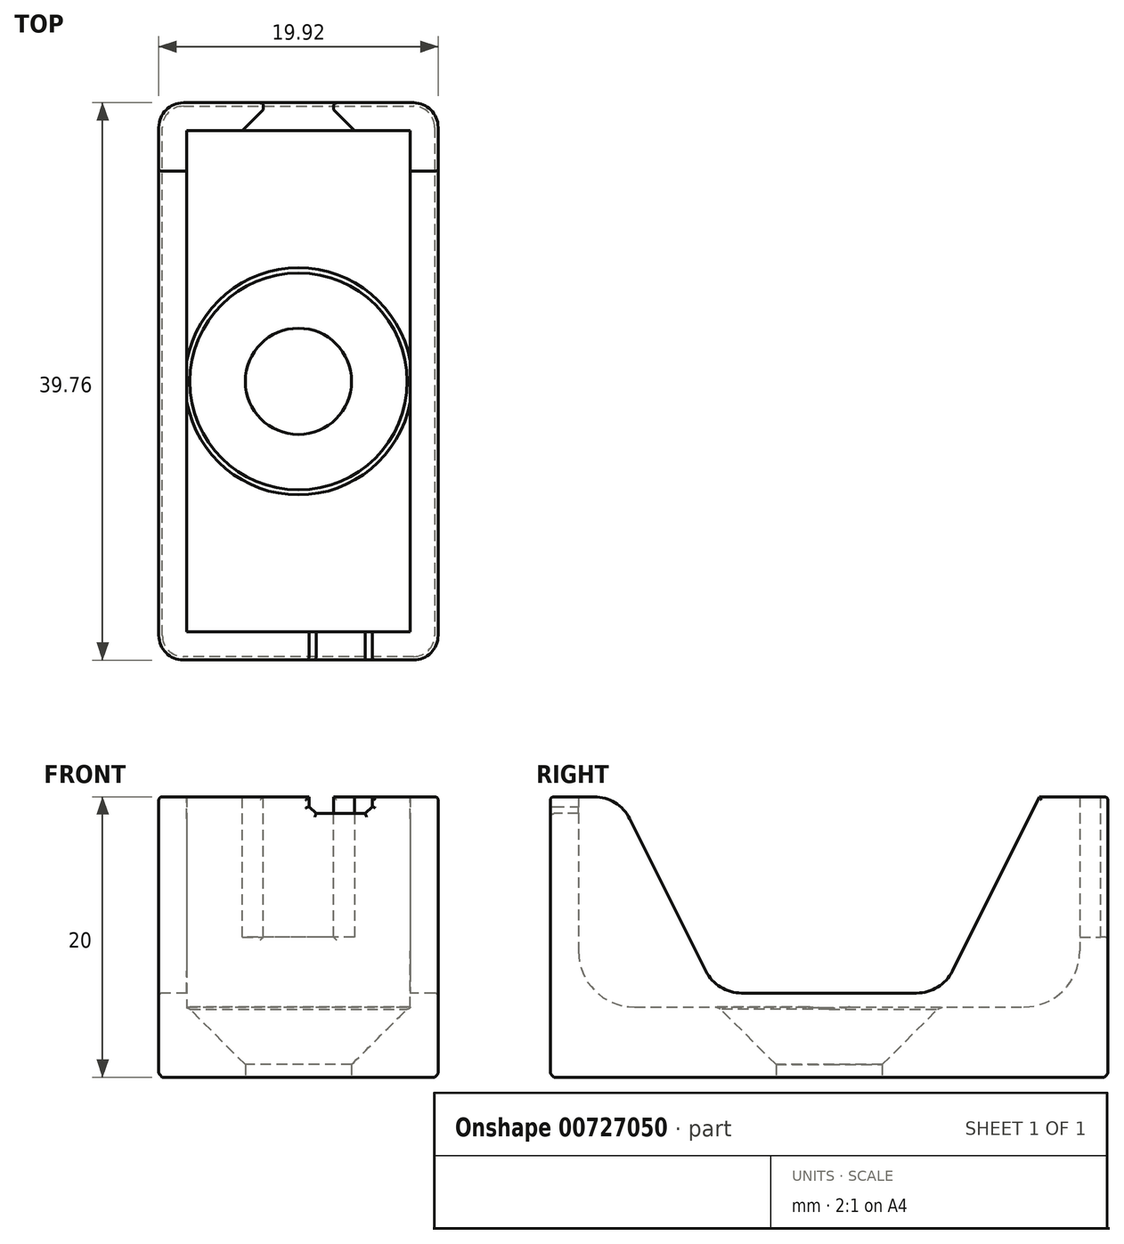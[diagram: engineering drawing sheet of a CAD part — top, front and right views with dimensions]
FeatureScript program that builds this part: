
annotation { "Feature Type Name" : "Feature", "Feature Type Description" : "" }
export const myFeature = defineFeature(function(context is Context, id is Id, definition is map)
    precondition{}
    {
        {
            var Q0;
            Q0=qCreatedBy(makeId("Top.planeOp"),FACE);
            var sketch = newSketch(context, id + "F0", { "sketchPlane" : qUnion([Q0])});
            skLineSegment(sketch, "E0.bottom", {"start": v(7.96, 17.88) * mm, "end": v(-7.96, 17.88) * mm});
            skLineSegment(sketch, "E0.top", {"start": v(7.96, -17.88) * mm, "end": v(-7.96, -17.88) * mm});
            skLineSegment(sketch, "E0.left", {"start": v(7.96, 17.88) * mm, "end": v(7.96, -17.88) * mm});
            skLineSegment(sketch, "E0.right", {"start": v(-7.96, 17.88) * mm, "end": v(-7.96, -17.88) * mm});
            skPoint(sketch, "E0.middle", {"position": v(0, 0) * mm});
            skLineSegment(sketch, "E1.0", {"start": v(9.96, 19.88) * mm, "end": v(-9.96, 19.88) * mm});
            skLineSegment(sketch, "E1.1", {"start": v(9.96, 19.88) * mm, "end": v(9.96, -19.88) * mm});
            skLineSegment(sketch, "E1.2", {"start": v(9.96, -19.88) * mm, "end": v(-9.96, -19.88) * mm});
            skLineSegment(sketch, "E1.3", {"start": v(-9.96, 19.88) * mm, "end": v(-9.96, -19.88) * mm});
            skCircle(sketch, "E2", {"center": v(0, 0) * mm, "radius": 3.8 * mm});
            skSolve(sketch);
        }
        {
            var Q0;
            Q0=makeQuery(id+"F0.imprint","IMPRINT",FACE,{"disambiguationData":[TD([[makeQuery(id+"F0.imprint","IMPRINT",EDGE,{"derivedFrom":sQuery(id+"F0.wireOp",EDGE,"E0.bottom")}),1.0]])]});
            var Q1;
            Q1=makeQuery(id+"F0.imprint","IMPRINT",FACE,{"disambiguationData":[TD([[makeQuery(id+"F0.imprint","IMPRINT",EDGE,{"derivedFrom":sQuery(id+"F0.wireOp",EDGE,"E0.bottom")}),-1.0]])]});
            extrude(context, id + "F1", {"entities" : qUnion([Q0, Q1]), "depth" : 5 * mm, "offsetDistance" : 25 * mm});
        }
        {
            var Q0;
            Q0=makeQuery(id+"F0.imprint","IMPRINT",FACE,{"disambiguationData":[TD([[makeQuery(id+"F0.imprint","IMPRINT",EDGE,{"derivedFrom":sQuery(id+"F0.wireOp",EDGE,"E0.bottom")}),-1.0]])]});
            extrude(context, id + "F2", {"entities" : qUnion([Q0]), "operationType" : NewBodyOperationType.ADD, "depth" : 20 * mm, "offsetDistance" : 25 * mm});
        }
        {
            var Q0;
            Q0=makeQuery(id+"F1.opExtrude","CAP_FACE",FACE,{"disambiguationData":[OSD([sQuery(id+"F0.wireOp",EDGE,"E1.0"),sQuery(id+"F0.wireOp",EDGE,"E1.1"),sQuery(id+"F0.wireOp",EDGE,"E1.2"),sQuery(id+"F0.wireOp",EDGE,"E1.3"),sQuery(id+"F0.wireOp",EDGE,"E2")])],"isStart":false});
            var sketch = newSketch(context, id + "F3", { "sketchPlane" : qUnion([Q0])});
            skLineSegment(sketch, "E3", {"start": v(7.96, -17.88) * mm, "end": v(5.26, -17.88) * mm});
            skLineSegment(sketch, "E4", {"start": v(5.26, -17.88) * mm, "end": v(0.76, -17.88) * mm});
            skLineSegment(sketch, "E5", {"start": v(0.76, -17.88) * mm, "end": v(0.76, -20.5) * mm});
            skLineSegment(sketch, "E6", {"start": v(0.76, -20.5) * mm, "end": v(5.26, -20.5) * mm});
            skLineSegment(sketch, "E7", {"start": v(5.26, -20.5) * mm, "end": v(5.26, -17.88) * mm});
            skSolve(sketch);
        }
        {
            var Q0;
            Q0 = qSketchRegion(id + "F3", true);
            extrude(context, id + "F4", {"entities" : qUnion([Q0]), "operationType" : NewBodyOperationType.REMOVE, "depth" : 35.9 * mm, "offsetDistance" : 25 * mm, "hasSecondDirection" : true, "secondDirectionOppositeDirection" : false, "secondDirectionDepth" : 13.8 * mm});
        }
        {
            var Q0;
            Q0=makeQuery(id+"F1.opExtrude","CAP_FACE",FACE,{"disambiguationData":[OSD([sQuery(id+"F0.wireOp",EDGE,"E1.0"),sQuery(id+"F0.wireOp",EDGE,"E1.1"),sQuery(id+"F0.wireOp",EDGE,"E1.2"),sQuery(id+"F0.wireOp",EDGE,"E1.3"),sQuery(id+"F0.wireOp",EDGE,"E2")])],"isStart":false});
            var sketch = newSketch(context, id + "F5", { "sketchPlane" : qUnion([Q0])});
            skLineSegment(sketch, "E8.bottom", {"start": v(2.5, 20.25) * mm, "end": v(-2.5, 20.25) * mm});
            skLineSegment(sketch, "E8.top", {"start": v(2.5, 17.25) * mm, "end": v(-2.5, 17.25) * mm});
            skLineSegment(sketch, "E8.left", {"start": v(2.5, 20.25) * mm, "end": v(2.5, 17.25) * mm});
            skLineSegment(sketch, "E8.right", {"start": v(-2.5, 20.25) * mm, "end": v(-2.5, 17.25) * mm});
            skPoint(sketch, "E8.middle", {"position": v(0, 18.75) * mm});
            skSolve(sketch);
        }
        {
            var Q0;
            Q0 = qSketchRegion(id + "F5", true);
            extrude(context, id + "F6", {"entities" : qUnion([Q0]), "operationType" : NewBodyOperationType.REMOVE, "depth" : 20 * mm, "offsetDistance" : 25 * mm, "hasSecondDirection" : true, "secondDirectionOppositeDirection" : false, "secondDirectionDepth" : 5 * mm});
        }
        {
            var Q0;
            {var subQ0=sQuery(id+"F0.wireOp",EDGE,"E1.3");Q0=makeQuery(id+"F2.boolean.opBoolean","MERGE",FACE,{"derivedFrom":[makeQuery(id+"F1.opExtrude","SWEPT_FACE",FACE,{"disambiguationData":[OSD([subQ0])]}),makeQuery(id+"F2.opExtrude","SWEPT_FACE",FACE,{"disambiguationData":[OSD([subQ0])]})]});}
            var sketch = newSketch(context, id + "F7", { "sketchPlane" : qUnion([Q0])});
            skLineSegment(sketch, "E9", {"start": v(0, 0) * mm, "end": v(0, 6) * mm});
            skLineSegment(sketch, "E10", {"start": v(0, 20) * mm, "end": v(-15, 20) * mm});
            skLineSegment(sketch, "E11", {"start": v(0, 20) * mm, "end": v(15, 20) * mm});
            skLineSegment(sketch, "E12", {"start": v(0, 6) * mm, "end": v(8, 6) * mm});
            skLineSegment(sketch, "E13", {"start": v(8, 6) * mm, "end": v(15, 20) * mm});
            skLineSegment(sketch, "E14", {"start": v(0, 6) * mm, "end": v(-8, 6) * mm});
            skLineSegment(sketch, "E15", {"start": v(-8, 6) * mm, "end": v(-15, 20) * mm});
            skSolve(sketch);
        }
        {
            var Q0;
            Q0=makeQuery(id+"F7.imprint","IMPRINT",FACE,{"disambiguationData":[TD([[makeQuery(id+"F7.imprint","IMPRINT",EDGE,{"derivedFrom":sQuery(id+"F7.wireOp",EDGE,"E10")}),-1.0]])]});
            extrude(context, id + "F8", {"entities" : qUnion([Q0]), "operationType" : NewBodyOperationType.REMOVE, "oppositeDirection" : true, "depth" : 25 * mm, "offsetDistance" : 25 * mm});
        }
        {
            var Q0;
            Q0=makeQuery(id+"F1.opExtrude","CAP_EDGE",EDGE,{"disambiguationData":[OSD([sQuery(id+"F0.wireOp",EDGE,"E2")])],"isStart":false});
            chamfer(context, id + "F9", {"entities" : qUnion([Q0]), "width" : 4.1 * mm, "tangentPropagation" : true});
        }
        {
            var Q0;
            {var subQ0=sQuery(id+"F0.wireOp",EDGE,"E1.3");var subQ1=sQuery(id+"F0.wireOp",EDGE,"E1.0");Q0=makeQuery(id+"F2.boolean.opBoolean","MERGE",EDGE,{"derivedFrom":[makeQuery(id+"F1.opExtrude","SWEPT_EDGE",EDGE,{"disambiguationData":[OSD([subQ1,subQ0])]}),makeQuery(id+"F2.opExtrude","SWEPT_EDGE",EDGE,{"disambiguationData":[OSD([subQ1,subQ0])]})]});}
            var Q1;
            {var subQ0=sQuery(id+"F0.wireOp",EDGE,"E1.1");var subQ1=sQuery(id+"F0.wireOp",EDGE,"E1.0");Q1=makeQuery(id+"F2.boolean.opBoolean","MERGE",EDGE,{"derivedFrom":[makeQuery(id+"F1.opExtrude","SWEPT_EDGE",EDGE,{"disambiguationData":[OSD([subQ1,subQ0])]}),makeQuery(id+"F2.opExtrude","SWEPT_EDGE",EDGE,{"disambiguationData":[OSD([subQ1,subQ0])]})]});}
            var Q2;
            {var subQ0=sQuery(id+"F0.wireOp",EDGE,"E1.2");var subQ1=sQuery(id+"F0.wireOp",EDGE,"E1.1");Q2=makeQuery(id+"F2.boolean.opBoolean","MERGE",EDGE,{"derivedFrom":[makeQuery(id+"F1.opExtrude","SWEPT_EDGE",EDGE,{"disambiguationData":[OSD([subQ1,subQ0])]}),makeQuery(id+"F2.opExtrude","SWEPT_EDGE",EDGE,{"disambiguationData":[OSD([subQ1,subQ0])]})]});}
            var Q3;
            {var subQ0=sQuery(id+"F0.wireOp",EDGE,"E1.3");var subQ1=sQuery(id+"F0.wireOp",EDGE,"E1.2");Q3=makeQuery(id+"F2.boolean.opBoolean","MERGE",EDGE,{"derivedFrom":[makeQuery(id+"F1.opExtrude","SWEPT_EDGE",EDGE,{"disambiguationData":[OSD([subQ1,subQ0])]}),makeQuery(id+"F2.opExtrude","SWEPT_EDGE",EDGE,{"disambiguationData":[OSD([subQ1,subQ0])]})]});}
            fillet(context, id + "F10", {"entities" : qUnion([Q0, Q1, Q2, Q3]), "radius" : 1.75 * mm, "tangentPropagation" : true, "allowEdgeOverflow" : false});
        }
        {
            var Q0;
            Q0=makeQuery(id+"F2.boolean.opBoolean","INTERSECT",EDGE,{"derivedFrom":[makeQuery(id+"F1.opExtrude","CAP_FACE",FACE,{"disambiguationData":[OSD([sQuery(id+"F0.wireOp",EDGE,"E1.0"),sQuery(id+"F0.wireOp",EDGE,"E1.1"),sQuery(id+"F0.wireOp",EDGE,"E1.2"),sQuery(id+"F0.wireOp",EDGE,"E1.3"),sQuery(id+"F0.wireOp",EDGE,"E2")])],"isStart":false}),makeQuery(id+"F2.opExtrude","SWEPT_FACE",FACE,{"disambiguationData":[OSD([sQuery(id+"F0.wireOp",EDGE,"E0.bottom")])]})]});
            var Q1;
            Q1=makeQuery(id+"F2.boolean.opBoolean","INTERSECT",EDGE,{"derivedFrom":[makeQuery(id+"F1.opExtrude","CAP_FACE",FACE,{"disambiguationData":[OSD([sQuery(id+"F0.wireOp",EDGE,"E1.0"),sQuery(id+"F0.wireOp",EDGE,"E1.1"),sQuery(id+"F0.wireOp",EDGE,"E1.2"),sQuery(id+"F0.wireOp",EDGE,"E1.3"),sQuery(id+"F0.wireOp",EDGE,"E2")])],"isStart":false}),makeQuery(id+"F2.opExtrude","SWEPT_FACE",FACE,{"disambiguationData":[OSD([sQuery(id+"F0.wireOp",EDGE,"E0.top")])]})]});
            fillet(context, id + "F11", {"entities" : qUnion([Q0, Q1]), "radius" : 4 * mm, "tangentPropagation" : true, "allowEdgeOverflow" : false});
        }
        {
            var Q0;
            Q0=makeQuery(id+"F4.boolean.opBoolean","COPY",EDGE,{"derivedFrom":makeQuery(id+"F4.opExtrude","CAP_EDGE",EDGE,{"disambiguationData":[OSD([sQuery(id+"F3.wireOp",EDGE,"E5")])],"isStart":true})});
            var Q1;
            Q1=makeQuery(id+"F4.boolean.opBoolean","COPY",EDGE,{"derivedFrom":makeQuery(id+"F4.opExtrude","CAP_EDGE",EDGE,{"disambiguationData":[OSD([sQuery(id+"F3.wireOp",EDGE,"E7")])],"isStart":true})});
            var Q2;
            {var subQ0=sQuery(id+"F0.wireOp",EDGE,"E2");Q2=makeQuery(id+"F9.opChamfer","BLEND_EDGE",EDGE,{"blendedFrom":[makeQuery(id+"F1.opExtrude","CAP_EDGE",EDGE,{"disambiguationData":[OSD([subQ0])],"isStart":false}),makeQuery(id+"F1.opExtrude","CAP_FACE",FACE,{"disambiguationData":[OSD([sQuery(id+"F0.wireOp",EDGE,"E1.0"),sQuery(id+"F0.wireOp",EDGE,"E1.1"),sQuery(id+"F0.wireOp",EDGE,"E1.2"),sQuery(id+"F0.wireOp",EDGE,"E1.3"),subQ0])],"isStart":false})],"blendedInto":[makeQuery(id+"F1.opExtrude","CAP_FACE",FACE,{"disambiguationData":[OSD([sQuery(id+"F0.wireOp",EDGE,"E1.0"),sQuery(id+"F0.wireOp",EDGE,"E1.1"),sQuery(id+"F0.wireOp",EDGE,"E1.2"),sQuery(id+"F0.wireOp",EDGE,"E1.3"),subQ0])],"isStart":false})]});}
            chamfer(context, id + "F12", {"entities" : qUnion([Q0, Q1, Q2]), "width" : .5 * mm, "tangentPropagation" : true});
        }
        {
            var Q0;
            Q0=makeQuery(id+"F6.boolean.opBoolean","INTERSECT",EDGE,{"derivedFrom":[makeQuery(id+"F2.opExtrude","SWEPT_FACE",FACE,{"disambiguationData":[OSD([sQuery(id+"F0.wireOp",EDGE,"E0.bottom")])]}),makeQuery(id+"F6.opExtrude","SWEPT_FACE",FACE,{"disambiguationData":[OSD([sQuery(id+"F5.wireOp",EDGE,"E8.right")])]})]});
            var Q1;
            Q1=makeQuery(id+"F6.boolean.opBoolean","INTERSECT",EDGE,{"derivedFrom":[makeQuery(id+"F2.opExtrude","SWEPT_FACE",FACE,{"disambiguationData":[OSD([sQuery(id+"F0.wireOp",EDGE,"E0.bottom")])]}),makeQuery(id+"F6.opExtrude","SWEPT_FACE",FACE,{"disambiguationData":[OSD([sQuery(id+"F5.wireOp",EDGE,"E8.left")])]})]});
            chamfer(context, id + "F13", {"entities" : qUnion([Q0, Q1]), "width" : 1.5 * mm, "tangentPropagation" : true});
        }
        {
            var Q0;
            {var subQ0=sQuery(id+"F7.wireOp",EDGE,"E12");var subQ1=sQuery(id+"F0.wireOp",EDGE,"E1.3");var subQ2=sQuery(id+"F7.wireOp",EDGE,"E13");Q0=makeQuery(id+"F8.boolean.opBoolean","COPY",EDGE,{"disambiguationData":[TD([makeQuery(id+"F1.opExtrude","SWEPT_FACE",FACE,{"disambiguationData":[OSD([subQ1])]})])],"derivedFrom":makeQuery(id+"F8.opExtrude","SWEPT_EDGE",EDGE,{"disambiguationData":[OSD([subQ0,subQ2])]})});}
            var Q1;
            {var subQ1=sQuery(id+"F0.wireOp",EDGE,"E1.3");var subQ2=sQuery(id+"F7.wireOp",EDGE,"E13");Q1=makeQuery(id+"F8.boolean.opBoolean","COPY",EDGE,{"disambiguationData":[TD([makeQuery(id+"F1.opExtrude","SWEPT_FACE",FACE,{"disambiguationData":[OSD([subQ1])]})])],"derivedFrom":makeQuery(id+"F8.opExtrude","SWEPT_EDGE",EDGE,{"disambiguationData":[OSD([subQ1,sQuery(id+"F7.wireOp",EDGE,"E11"),subQ2])]})});}
            var Q2;
            {var subQ1=sQuery(id+"F0.wireOp",EDGE,"E1.1");var subQ2=sQuery(id+"F0.wireOp",EDGE,"E1.3");var subQ3=sQuery(id+"F7.wireOp",EDGE,"E13");Q2=makeQuery(id+"F8.boolean.opBoolean","COPY",EDGE,{"disambiguationData":[TD([makeQuery(id+"F1.opExtrude","SWEPT_FACE",FACE,{"disambiguationData":[OSD([subQ1])]})])],"derivedFrom":makeQuery(id+"F8.opExtrude","SWEPT_EDGE",EDGE,{"disambiguationData":[OSD([subQ2,sQuery(id+"F7.wireOp",EDGE,"E11"),subQ3])]})});}
            var Q3;
            {var subQ0=sQuery(id+"F7.wireOp",EDGE,"E12");var subQ1=sQuery(id+"F0.wireOp",EDGE,"E1.1");var subQ2=sQuery(id+"F7.wireOp",EDGE,"E13");Q3=makeQuery(id+"F8.boolean.opBoolean","COPY",EDGE,{"disambiguationData":[TD([makeQuery(id+"F1.opExtrude","SWEPT_FACE",FACE,{"disambiguationData":[OSD([subQ1])]})])],"derivedFrom":makeQuery(id+"F8.opExtrude","SWEPT_EDGE",EDGE,{"disambiguationData":[OSD([subQ0,subQ2])]})});}
            var Q4;
            {var subQ0=sQuery(id+"F7.wireOp",EDGE,"E14");var subQ1=sQuery(id+"F0.wireOp",EDGE,"E1.1");var subQ2=sQuery(id+"F7.wireOp",EDGE,"E15");Q4=makeQuery(id+"F8.boolean.opBoolean","COPY",EDGE,{"disambiguationData":[TD([makeQuery(id+"F1.opExtrude","SWEPT_FACE",FACE,{"disambiguationData":[OSD([subQ1])]})])],"derivedFrom":makeQuery(id+"F8.opExtrude","SWEPT_EDGE",EDGE,{"disambiguationData":[OSD([subQ0,subQ2])]})});}
            var Q5;
            {var subQ0=sQuery(id+"F7.wireOp",EDGE,"E14");var subQ1=sQuery(id+"F0.wireOp",EDGE,"E1.3");var subQ2=sQuery(id+"F7.wireOp",EDGE,"E15");Q5=makeQuery(id+"F8.boolean.opBoolean","COPY",EDGE,{"disambiguationData":[TD([makeQuery(id+"F1.opExtrude","SWEPT_FACE",FACE,{"disambiguationData":[OSD([subQ1])]})])],"derivedFrom":makeQuery(id+"F8.opExtrude","SWEPT_EDGE",EDGE,{"disambiguationData":[OSD([subQ0,subQ2])]})});}
            var Q6;
            {var subQ1=sQuery(id+"F0.wireOp",EDGE,"E1.3");var subQ2=sQuery(id+"F7.wireOp",EDGE,"E15");Q6=makeQuery(id+"F8.boolean.opBoolean","COPY",EDGE,{"disambiguationData":[TD([makeQuery(id+"F1.opExtrude","SWEPT_FACE",FACE,{"disambiguationData":[OSD([subQ1])]})])],"derivedFrom":makeQuery(id+"F8.opExtrude","SWEPT_EDGE",EDGE,{"disambiguationData":[OSD([subQ1,sQuery(id+"F7.wireOp",EDGE,"E10"),subQ2])]})});}
            var Q7;
            {var subQ1=sQuery(id+"F0.wireOp",EDGE,"E1.1");var subQ2=sQuery(id+"F0.wireOp",EDGE,"E1.3");var subQ3=sQuery(id+"F7.wireOp",EDGE,"E15");Q7=makeQuery(id+"F8.boolean.opBoolean","COPY",EDGE,{"disambiguationData":[TD([makeQuery(id+"F1.opExtrude","SWEPT_FACE",FACE,{"disambiguationData":[OSD([subQ1])]})])],"derivedFrom":makeQuery(id+"F8.opExtrude","SWEPT_EDGE",EDGE,{"disambiguationData":[OSD([subQ2,sQuery(id+"F7.wireOp",EDGE,"E10"),subQ3])]})});}
            fillet(context, id + "F14", {"entities" : qUnion([Q0, Q1, Q2, Q3, Q4, Q5, Q6, Q7]), "radius" : 2.85 * mm, "tangentPropagation" : true, "allowEdgeOverflow" : false});
        }
        {
            var Q0;
            {var subQ0=sQuery(id+"F0.wireOp",EDGE,"E1.2");var subQ1=sQuery(id+"F0.wireOp",EDGE,"E1.1");Q0=makeQuery(id+"F10.opFillet","BLEND_EDGE",EDGE,{"blendedFrom":[makeQuery(id+"F2.boolean.opBoolean","MERGE",EDGE,{"derivedFrom":[makeQuery(id+"F1.opExtrude","SWEPT_EDGE",EDGE,{"disambiguationData":[OSD([subQ1,subQ0])]}),makeQuery(id+"F2.opExtrude","SWEPT_EDGE",EDGE,{"disambiguationData":[OSD([subQ1,subQ0])]})]}),makeQuery(id+"F1.opExtrude","CAP_FACE",FACE,{"disambiguationData":[OSD([sQuery(id+"F0.wireOp",EDGE,"E1.0"),subQ1,subQ0,sQuery(id+"F0.wireOp",EDGE,"E1.3"),sQuery(id+"F0.wireOp",EDGE,"E2")])],"isStart":true})],"blendedInto":[makeQuery(id+"F1.opExtrude","CAP_FACE",FACE,{"disambiguationData":[OSD([sQuery(id+"F0.wireOp",EDGE,"E1.0"),subQ1,subQ0,sQuery(id+"F0.wireOp",EDGE,"E1.3"),sQuery(id+"F0.wireOp",EDGE,"E2")])],"isStart":true})]});}
            var Q1;
            Q1=makeQuery(id+"F1.opExtrude","CAP_EDGE",EDGE,{"disambiguationData":[OSD([sQuery(id+"F0.wireOp",EDGE,"E1.1")])],"isStart":true});
            var Q2;
            Q2=makeQuery(id+"F1.opExtrude","CAP_EDGE",EDGE,{"disambiguationData":[OSD([sQuery(id+"F0.wireOp",EDGE,"E1.2")])],"isStart":true});
            var Q3;
            {var subQ0=sQuery(id+"F0.wireOp",EDGE,"E1.3");var subQ1=sQuery(id+"F0.wireOp",EDGE,"E1.2");Q3=makeQuery(id+"F10.opFillet","BLEND_EDGE",EDGE,{"blendedFrom":[makeQuery(id+"F2.boolean.opBoolean","MERGE",EDGE,{"derivedFrom":[makeQuery(id+"F1.opExtrude","SWEPT_EDGE",EDGE,{"disambiguationData":[OSD([subQ1,subQ0])]}),makeQuery(id+"F2.opExtrude","SWEPT_EDGE",EDGE,{"disambiguationData":[OSD([subQ1,subQ0])]})]}),makeQuery(id+"F1.opExtrude","CAP_FACE",FACE,{"disambiguationData":[OSD([sQuery(id+"F0.wireOp",EDGE,"E1.0"),sQuery(id+"F0.wireOp",EDGE,"E1.1"),subQ1,subQ0,sQuery(id+"F0.wireOp",EDGE,"E2")])],"isStart":true})],"blendedInto":[makeQuery(id+"F1.opExtrude","CAP_FACE",FACE,{"disambiguationData":[OSD([sQuery(id+"F0.wireOp",EDGE,"E1.0"),sQuery(id+"F0.wireOp",EDGE,"E1.1"),subQ1,subQ0,sQuery(id+"F0.wireOp",EDGE,"E2")])],"isStart":true})]});}
            var Q4;
            Q4=makeQuery(id+"F1.opExtrude","CAP_EDGE",EDGE,{"disambiguationData":[OSD([sQuery(id+"F0.wireOp",EDGE,"E1.3")])],"isStart":true});
            var Q5;
            Q5=makeQuery(id+"F1.opExtrude","CAP_EDGE",EDGE,{"disambiguationData":[OSD([sQuery(id+"F0.wireOp",EDGE,"E1.0")])],"isStart":true});
            var Q6;
            {var subQ0=sQuery(id+"F0.wireOp",EDGE,"E1.3");var subQ1=sQuery(id+"F0.wireOp",EDGE,"E1.0");Q6=makeQuery(id+"F10.opFillet","BLEND_EDGE",EDGE,{"blendedFrom":[makeQuery(id+"F2.boolean.opBoolean","MERGE",EDGE,{"derivedFrom":[makeQuery(id+"F1.opExtrude","SWEPT_EDGE",EDGE,{"disambiguationData":[OSD([subQ1,subQ0])]}),makeQuery(id+"F2.opExtrude","SWEPT_EDGE",EDGE,{"disambiguationData":[OSD([subQ1,subQ0])]})]}),makeQuery(id+"F1.opExtrude","CAP_FACE",FACE,{"disambiguationData":[OSD([subQ1,sQuery(id+"F0.wireOp",EDGE,"E1.1"),sQuery(id+"F0.wireOp",EDGE,"E1.2"),subQ0,sQuery(id+"F0.wireOp",EDGE,"E2")])],"isStart":true})],"blendedInto":[makeQuery(id+"F1.opExtrude","CAP_FACE",FACE,{"disambiguationData":[OSD([subQ1,sQuery(id+"F0.wireOp",EDGE,"E1.1"),sQuery(id+"F0.wireOp",EDGE,"E1.2"),subQ0,sQuery(id+"F0.wireOp",EDGE,"E2")])],"isStart":true})]});}
            chamfer(context, id + "F15", {"entities" : qUnion([Q0, Q1, Q2, Q3, Q4, Q5, Q6]), "width" : .25 * mm, "tangentPropagation" : true});
        }
        {
            var Q0;
            {var subQ0=sQuery(id+"F0.wireOp",EDGE,"E1.3");var subQ1=sQuery(id+"F0.wireOp",EDGE,"E1.2");Q0=makeQuery(id+"F4.boolean.opBoolean","SPLIT",EDGE,{"disambiguationData":[TD([makeQuery(id+"F1.opExtrude","SWEPT_FACE",FACE,{"disambiguationData":[OSD([subQ0])]})])],"derivedFrom":makeQuery(id+"F2.opExtrude","CAP_EDGE",EDGE,{"disambiguationData":[OSD([subQ1])],"isStart":false})});}
            var Q1;
            {var subQ0=sQuery(id+"F0.wireOp",EDGE,"E0.right");var subQ2=sQuery(id+"F0.wireOp",EDGE,"E1.3");var subQ3=makeQuery(id+"F1.opExtrude","SWEPT_FACE",FACE,{"disambiguationData":[OSD([subQ2])]});var subQ4=sQuery(id+"F0.wireOp",EDGE,"E0.top");var subQ6=sQuery(id+"F0.wireOp",EDGE,"E1.2");var subQ7=makeQuery(id+"F1.opExtrude","SWEPT_FACE",FACE,{"disambiguationData":[OSD([subQ6])]});var subQ11=sQuery(id+"F0.wireOp",EDGE,"E0.bottom");var subQ12=sQuery(id+"F0.wireOp",EDGE,"E1.0");Q1=makeQuery(id+"F10.opFillet","BLEND_EDGE",EDGE,{"blendedFrom":[makeQuery(id+"F2.boolean.opBoolean","MERGE",EDGE,{"derivedFrom":[makeQuery(id+"F1.opExtrude","SWEPT_EDGE",EDGE,{"disambiguationData":[OSD([subQ6,subQ2])]}),makeQuery(id+"F2.opExtrude","SWEPT_EDGE",EDGE,{"disambiguationData":[OSD([subQ6,subQ2])]})]}),makeQuery(id+"F8.boolean.opBoolean","SPLIT",FACE,{"disambiguationData":[TD([subQ7])],"derivedFrom":makeQuery(id+"F6.boolean.opBoolean","SPLIT",FACE,{"disambiguationData":[TD([subQ3])],"derivedFrom":makeQuery(id+"F2.opExtrude","CAP_FACE",FACE,{"disambiguationData":[OSD([subQ11,subQ4,sQuery(id+"F0.wireOp",EDGE,"E0.left"),subQ0,subQ12,sQuery(id+"F0.wireOp",EDGE,"E1.1"),subQ6,subQ2])],"isStart":false})})})],"blendedInto":[makeQuery(id+"F8.boolean.opBoolean","SPLIT",FACE,{"disambiguationData":[TD([subQ7])],"derivedFrom":makeQuery(id+"F6.boolean.opBoolean","SPLIT",FACE,{"disambiguationData":[TD([subQ3])],"derivedFrom":makeQuery(id+"F2.opExtrude","CAP_FACE",FACE,{"disambiguationData":[OSD([subQ11,subQ4,sQuery(id+"F0.wireOp",EDGE,"E0.left"),subQ0,subQ12,sQuery(id+"F0.wireOp",EDGE,"E1.1"),subQ6,subQ2])],"isStart":false})})})]});}
            var Q2;
            {var subQ0=sQuery(id+"F0.wireOp",EDGE,"E1.2");Q2=makeQuery(id+"F4.boolean.opBoolean","INTERSECT",EDGE,{"derivedFrom":[makeQuery(id+"F2.boolean.opBoolean","MERGE",FACE,{"derivedFrom":[makeQuery(id+"F1.opExtrude","SWEPT_FACE",FACE,{"disambiguationData":[OSD([subQ0])]}),makeQuery(id+"F2.opExtrude","SWEPT_FACE",FACE,{"disambiguationData":[OSD([subQ0])]})]}),makeQuery(id+"F4.opExtrude","SWEPT_FACE",FACE,{"disambiguationData":[OSD([sQuery(id+"F3.wireOp",EDGE,"E5")])]})]});}
            var Q3;
            {var subQ0=sQuery(id+"F0.wireOp",EDGE,"E1.2");var subQ1=sQuery(id+"F0.wireOp",EDGE,"E1.1");Q3=makeQuery(id+"F4.boolean.opBoolean","SPLIT",EDGE,{"disambiguationData":[TD([makeQuery(id+"F1.opExtrude","SWEPT_FACE",FACE,{"disambiguationData":[OSD([subQ1])]})])],"derivedFrom":makeQuery(id+"F2.opExtrude","CAP_EDGE",EDGE,{"disambiguationData":[OSD([subQ0])],"isStart":false})});}
            var Q4;
            {var subQ0=sQuery(id+"F0.wireOp",EDGE,"E1.2");Q4=makeQuery(id+"F12.opChamfer","BLEND_EDGE",EDGE,{"blendedFrom":[makeQuery(id+"F4.boolean.opBoolean","COPY",EDGE,{"derivedFrom":makeQuery(id+"F4.opExtrude","CAP_EDGE",EDGE,{"disambiguationData":[OSD([sQuery(id+"F3.wireOp",EDGE,"E5")])],"isStart":true})}),makeQuery(id+"F2.boolean.opBoolean","MERGE",FACE,{"derivedFrom":[makeQuery(id+"F1.opExtrude","SWEPT_FACE",FACE,{"disambiguationData":[OSD([subQ0])]}),makeQuery(id+"F2.opExtrude","SWEPT_FACE",FACE,{"disambiguationData":[OSD([subQ0])]})]})],"blendedInto":[makeQuery(id+"F2.boolean.opBoolean","MERGE",FACE,{"derivedFrom":[makeQuery(id+"F1.opExtrude","SWEPT_FACE",FACE,{"disambiguationData":[OSD([subQ0])]}),makeQuery(id+"F2.opExtrude","SWEPT_FACE",FACE,{"disambiguationData":[OSD([subQ0])]})]})]});}
            var Q5;
            {var subQ0=sQuery(id+"F0.wireOp",EDGE,"E1.2");Q5=makeQuery(id+"F4.boolean.opBoolean","INTERSECT",EDGE,{"derivedFrom":[makeQuery(id+"F2.boolean.opBoolean","MERGE",FACE,{"derivedFrom":[makeQuery(id+"F1.opExtrude","SWEPT_FACE",FACE,{"disambiguationData":[OSD([subQ0])]}),makeQuery(id+"F2.opExtrude","SWEPT_FACE",FACE,{"disambiguationData":[OSD([subQ0])]})]}),makeQuery(id+"F4.opExtrude","CAP_FACE",FACE,{"disambiguationData":[OSD([sQuery(id+"F3.wireOp",EDGE,"E4"),sQuery(id+"F3.wireOp",EDGE,"E5"),sQuery(id+"F3.wireOp",EDGE,"E6"),sQuery(id+"F3.wireOp",EDGE,"E7")])],"isStart":true})]});}
            var Q6;
            {var subQ0=sQuery(id+"F0.wireOp",EDGE,"E1.2");Q6=makeQuery(id+"F12.opChamfer","BLEND_EDGE",EDGE,{"blendedFrom":[makeQuery(id+"F4.boolean.opBoolean","COPY",EDGE,{"derivedFrom":makeQuery(id+"F4.opExtrude","CAP_EDGE",EDGE,{"disambiguationData":[OSD([sQuery(id+"F3.wireOp",EDGE,"E7")])],"isStart":true})}),makeQuery(id+"F2.boolean.opBoolean","MERGE",FACE,{"derivedFrom":[makeQuery(id+"F1.opExtrude","SWEPT_FACE",FACE,{"disambiguationData":[OSD([subQ0])]}),makeQuery(id+"F2.opExtrude","SWEPT_FACE",FACE,{"disambiguationData":[OSD([subQ0])]})]})],"blendedInto":[makeQuery(id+"F2.boolean.opBoolean","MERGE",FACE,{"derivedFrom":[makeQuery(id+"F1.opExtrude","SWEPT_FACE",FACE,{"disambiguationData":[OSD([subQ0])]}),makeQuery(id+"F2.opExtrude","SWEPT_FACE",FACE,{"disambiguationData":[OSD([subQ0])]})]})]});}
            var Q7;
            {var subQ0=sQuery(id+"F0.wireOp",EDGE,"E1.2");Q7=makeQuery(id+"F4.boolean.opBoolean","INTERSECT",EDGE,{"derivedFrom":[makeQuery(id+"F2.boolean.opBoolean","MERGE",FACE,{"derivedFrom":[makeQuery(id+"F1.opExtrude","SWEPT_FACE",FACE,{"disambiguationData":[OSD([subQ0])]}),makeQuery(id+"F2.opExtrude","SWEPT_FACE",FACE,{"disambiguationData":[OSD([subQ0])]})]}),makeQuery(id+"F4.opExtrude","SWEPT_FACE",FACE,{"disambiguationData":[OSD([sQuery(id+"F3.wireOp",EDGE,"E7")])]})]});}
            var Q8;
            {var subQ0=sQuery(id+"F0.wireOp",EDGE,"E1.0");Q8=makeQuery(id+"F6.boolean.opBoolean","INTERSECT",EDGE,{"derivedFrom":[makeQuery(id+"F2.boolean.opBoolean","MERGE",FACE,{"derivedFrom":[makeQuery(id+"F1.opExtrude","SWEPT_FACE",FACE,{"disambiguationData":[OSD([subQ0])]}),makeQuery(id+"F2.opExtrude","SWEPT_FACE",FACE,{"disambiguationData":[OSD([subQ0])]})]}),makeQuery(id+"F6.opExtrude","SWEPT_FACE",FACE,{"disambiguationData":[OSD([sQuery(id+"F5.wireOp",EDGE,"E8.left")])]})]});}
            var Q9;
            {var subQ0=sQuery(id+"F0.wireOp",EDGE,"E1.0");Q9=makeQuery(id+"F2.boolean.opBoolean","MERGE",FACE,{"derivedFrom":[makeQuery(id+"F1.opExtrude","SWEPT_FACE",FACE,{"disambiguationData":[OSD([subQ0])]}),makeQuery(id+"F2.opExtrude","SWEPT_FACE",FACE,{"disambiguationData":[OSD([subQ0])]})]});}
            fillet(context, id + "F16", {"entities" : qUnion([Q0, Q1, Q2, Q3, Q4, Q5, Q6, Q7, Q8, Q9]), "radius" : 0.24 * mm, "tangentPropagation" : true, "allowEdgeOverflow" : false});
        }
    });
